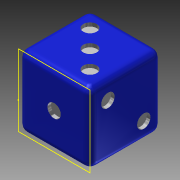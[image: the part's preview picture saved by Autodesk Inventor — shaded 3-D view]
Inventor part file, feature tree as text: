
AUTODESK INVENTOR PART (.ipt)
format: ipt  version: 2013 (Build 170138000, 138)  size: 252,928 bytes
history: native  units: in
note: dims shown in document units (in); Inventor stores cm internally (conversion verified against a paired STEP export)
features: sketch x8, extrude x7, fillet x2
ambient origin geometry x8: Origin, YZ Plane, XZ Plane, XY Plane, X Axis, Y Axis, Z Axis, Center Point
bodies: Solid1 (feature_tree)
feature tree (17):
  extrude  "Extrusion1"  Depth=1.0in
  sketch  "Sketch2"  dims[d2=1.0in d3=0.0in d4=0.187in]
  sketch  "Sketch3"  dims[d5=0.05in d6=0.0in d7=0.187in]
  extrude  "Extrusion2"  Depth=0.187in
  extrude  "Extrusion3"  Depth=0.187in
  extrude  "Extrusion4"  Depth=0.187in
  extrude  "Extrusion5"  Depth=0.187in
  extrude  "Extrusion6"  Depth=0.187in
  extrude  "Extrusion7"  Depth=0.05in TaperAngle=0.0deg
  fillet  "Fillet1"  Radius=0.187in
  fillet  "Fillet2"  Radius=0.187in
  sketch  "Sketch1"  dims[d0=1.0in d1=1.0in]
  sketch  "Sketch4"  dims[d8=0.187in d9=0.187in]
  sketch  "Sketch5"  dims[d10=0.05in d11=0.0in d12=0.187in]
  sketch  "Sketch6"  dims[d13=0.187in d14=0.187in]
  sketch  "Sketch7"  dims[d15=0.187in d16=0.05in d17=0.0in d18=0.187in d19=0.187in]
  sketch  "Sketch8"  dims[d20=0.187in d21=0.187in d22=0.187in d23=0.187in d24=0.05in d25=0.0in d26=0.25in d27=0.25in d28=0.25in d29=0.2498in d30=0.25in d31=0.2498in d32=0.25in d33=0.25in d34=0.5in d35=0.5in d36=0.187in d37=0.187in d38=0.187in d39=0.187in d40=0.187in d41=0.05in d42=0.0in d43=0.187in d44=0.187in d45=0.25in d46=0.25in d47=0.25in d48=0.25in d49=0.05in d50=0.0in d51=0.1in d52=0.1in]
